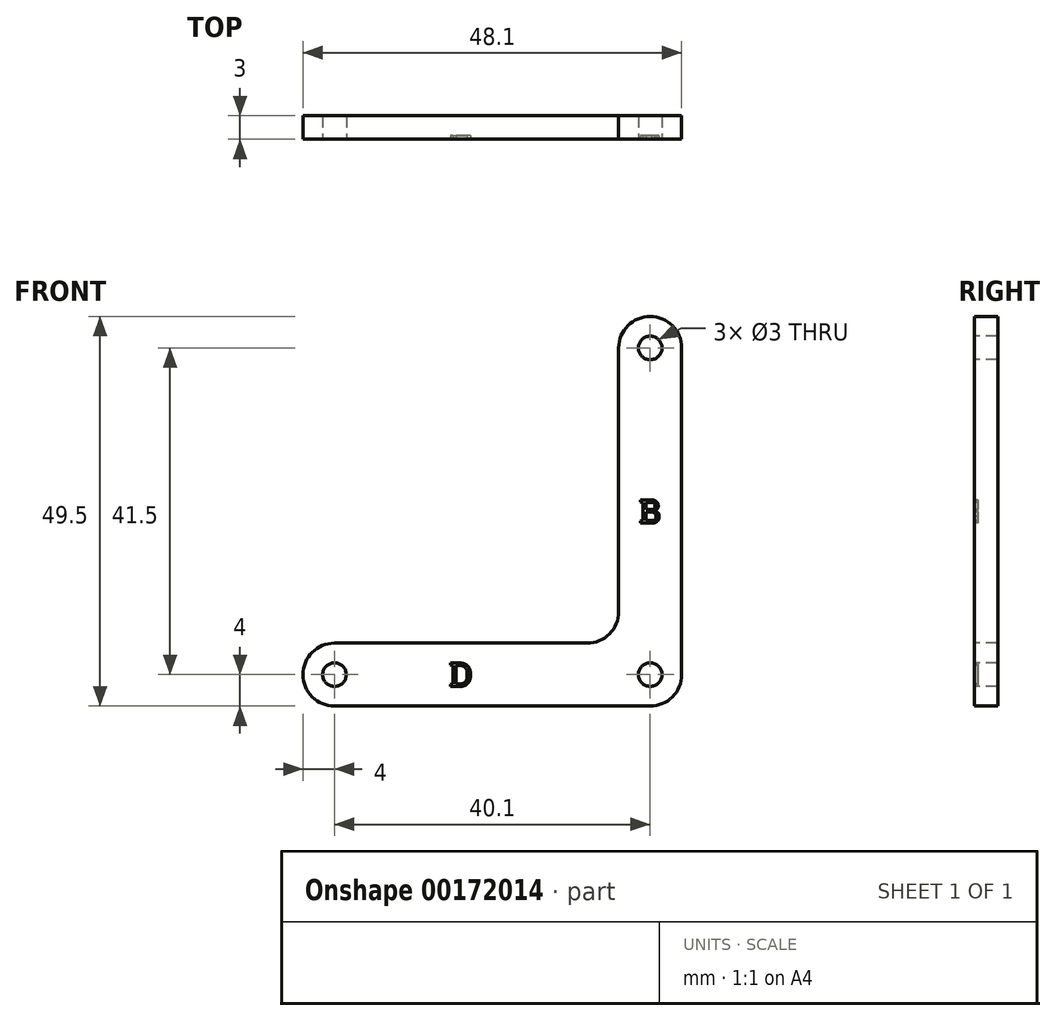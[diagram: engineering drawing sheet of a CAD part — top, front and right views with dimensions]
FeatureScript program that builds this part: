
annotation { "Feature Type Name" : "Feature", "Feature Type Description" : "" }
export const myFeature = defineFeature(function(context is Context, id is Id, definition is map)
    precondition{}
    {
        {
            assignVariable(context, id + "F0", {"name" : "Thickness", "anyValue" : 3});
        }
        {
            var Q0;
            Q0=qCreatedBy(makeId("Front.planeOp"),FACE);
            var sketch = newSketch(context, id + "F1", { "sketchPlane" : qUnion([Q0])});
            skCircle(sketch, "E0", {"center": v(-40.1, 0) * mm, "radius": 1.5 * mm});
            skCircle(sketch, "E1", {"center": v(0, 41.5) * mm, "radius": 1.5 * mm});
            skCircle(sketch, "E2", {"center": v(0, 0) * mm, "radius": 1.5 * mm});
            skArc(sketch, "E3", {"start": v(-40.1, 4) * mm, "mid": v(-44.1, 0) * mm, "end": v(-40.1, -4) * mm});
            skArc(sketch, "E4", {"start": v(4, 41.5) * mm, "mid": v(0, 45.5) * mm, "end": v(-4, 41.5) * mm});
            skArc(sketch, "E5", {"start": v(0, -4) * mm, "mid": v(2.83, -2.83) * mm, "end": v(4, 0) * mm});
            skArc(sketch, "E6", {"start": v(-8, 4) * mm, "mid": v(-5.17, 5.17) * mm, "end": v(-4, 8) * mm});
            skLineSegment(sketch, "E7", {"start": v(-40.1, 4) * mm, "end": v(-8, 4) * mm});
            skLineSegment(sketch, "E8", {"start": v(-4, 8) * mm, "end": v(-4, 41.5) * mm});
            skLineSegment(sketch, "E9", {"start": v(4, 41.5) * mm, "end": v(4, 0) * mm});
            skLineSegment(sketch, "E10", {"start": v(0, -4) * mm, "end": v(-40.1, -4) * mm});
            skSolve(sketch);
        }
        {
            var Q0;
            Q0=makeQuery(id+"F1.imprint","IMPRINT",FACE,{"disambiguationData":[TD([[makeQuery(id+"F1.imprint","IMPRINT",EDGE,{"derivedFrom":sQuery(id+"F1.wireOp",EDGE,"E0")}),-1.0]])]});
            extrude(context, id + "F2", {"entities" : qUnion([Q0]), "oppositeDirection" : true, "depth" : (getVariable(context, 'Thickness')) * mm});
        }
        {
            var Q0;
            Q0=qCreatedBy(makeId("Front.planeOp"),FACE);
            var sketch = newSketch(context, id + "F3", { "sketchPlane" : qUnion([Q0])});
            skText(sketch, "E11", { "text": "B", "fontName": "RobotoSlab-Regular.ttf"});
            skText(sketch, "E12", { "text": "D", "fontName": "RobotoSlab-Regular.ttf"});
            skLineSegment(sketch, "E13", {"start": v(-25.51, 0) * mm, "end": v(-22.59, 0) * mm, "construction": true});
            skLineSegment(sketch, "E14", {"start": v(1.4, 20.75) * mm, "end": v(4, 20.75) * mm, "construction": true});
            skLineSegment(sketch, "E15", {"start": v(-24.05, 4) * mm, "end": v(-24.05, 1.5) * mm, "construction": true});
            const initialGuessF3  = {"E11": [-0.0014, 0.01925, 1, 0, 0.003], "E12": [-0.02551, -0.0015, 1, 0, 0.003]};
            skSetInitialGuess(sketch, initialGuessF3);
            skSolve(sketch);
        }
        {
            assignVariable(context, id + "F4", {"name" : "DepthText", "anyValue" : .5});
        }
        {
            var Q0;
            Q0 = qSketchRegion(id + "F3", true);
            extrude(context, id + "F5", {"entities" : qUnion([Q0]), "operationType" : NewBodyOperationType.REMOVE, "oppositeDirection" : true, "depth" : (getVariable(context, 'DepthText')) * mm});
        }
    });
